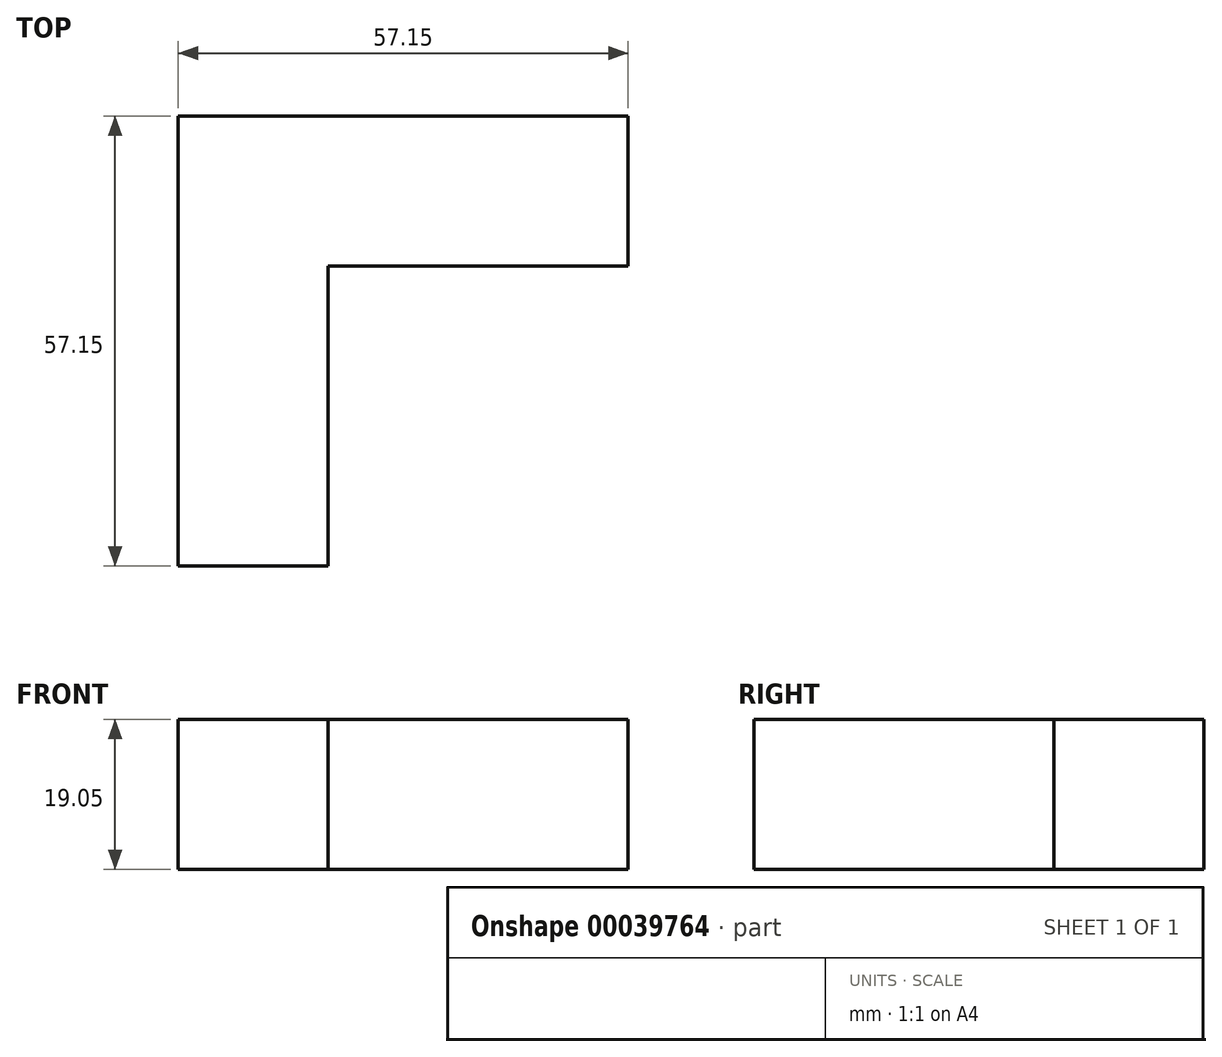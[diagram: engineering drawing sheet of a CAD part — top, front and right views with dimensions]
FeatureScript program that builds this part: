
annotation { "Feature Type Name" : "Feature", "Feature Type Description" : "" }
export const myFeature = defineFeature(function(context is Context, id is Id, definition is map)
    precondition{}
    {
        {
            var Q0;
            Q0=qCreatedBy(makeId("Top.planeOp"),FACE);
            var sketch = newSketch(context, id + "F0", { "sketchPlane" : qUnion([Q0])});
            skLineSegment(sketch, "E0.bottom", {"start": v(0, 0) * mm, "end": v(19.05, 0) * mm});
            skLineSegment(sketch, "E0.top", {"start": v(0, -19.05) * mm, "end": v(19.05, -19.05) * mm});
            skLineSegment(sketch, "E0.left", {"start": v(0, 0) * mm, "end": v(0, -19.05) * mm});
            skLineSegment(sketch, "E0.right", {"start": v(19.05, 0) * mm, "end": v(19.05, -19.05) * mm});
            skSolve(sketch);
        }
        {
            var Q0;
            Q0=makeQuery(id+"F0.imprint","IMPRINT",FACE,{"disambiguationData":[TD([[makeQuery(id+"F0.imprint","IMPRINT",EDGE,{"derivedFrom":sQuery(id+"F0.wireOp",EDGE,"E0.bottom")}),-1.0]])]});
            extrude(context, id + "F1", {"entities" : qUnion([Q0]), "depth" : 19.05 * mm});
        }
        {
            var Q0;
            Q0=makeQuery(id+"F1.opExtrude","SWEPT_FACE",FACE,{"disambiguationData":[OSD([sQuery(id+"F0.wireOp",EDGE,"E0.top")])]});
            extrude(context, id + "F2", {"entities" : qUnion([Q0]), "operationType" : NewBodyOperationType.ADD, "depth" : 38.1 * mm});
        }
        {
            var Q0;
            {var subQ0=sQuery(id+"F0.wireOp",EDGE,"E0.right");Q0=makeQuery(id+"F2.boolean.opBoolean","MERGE",FACE,{"derivedFrom":[makeQuery(id+"F1.opExtrude","SWEPT_FACE",FACE,{"disambiguationData":[OSD([subQ0])]}),makeQuery(id+"F2.opExtrude","SWEPT_FACE",FACE,{"disambiguationData":[OSD([sQuery(id+"F0.wireOp",EDGE,"E0.top"),subQ0])]})]});}
            var sketch = newSketch(context, id + "F3", { "sketchPlane" : qUnion([Q0])});
            skLineSegment(sketch, "E1.bottom", {"start": v(0, 0) * mm, "end": v(-19.05, 0) * mm});
            skLineSegment(sketch, "E1.top", {"start": v(0, 19.05) * mm, "end": v(-19.05, 19.05) * mm});
            skLineSegment(sketch, "E1.left", {"start": v(0, 0) * mm, "end": v(0, 19.05) * mm});
            skLineSegment(sketch, "E1.right", {"start": v(-19.05, 0) * mm, "end": v(-19.05, 19.05) * mm});
            skSolve(sketch);
        }
        {
            var Q0;
            Q0=makeQuery(id+"F3.imprint","IMPRINT",FACE,{"disambiguationData":[TD([[makeQuery(id+"F3.imprint","IMPRINT",EDGE,{"derivedFrom":sQuery(id+"F3.wireOp",EDGE,"E1.bottom")}),-1.0]])]});
            extrude(context, id + "F4", {"entities" : qUnion([Q0]), "operationType" : NewBodyOperationType.ADD, "depth" : 38.1 * mm});
        }
    });
